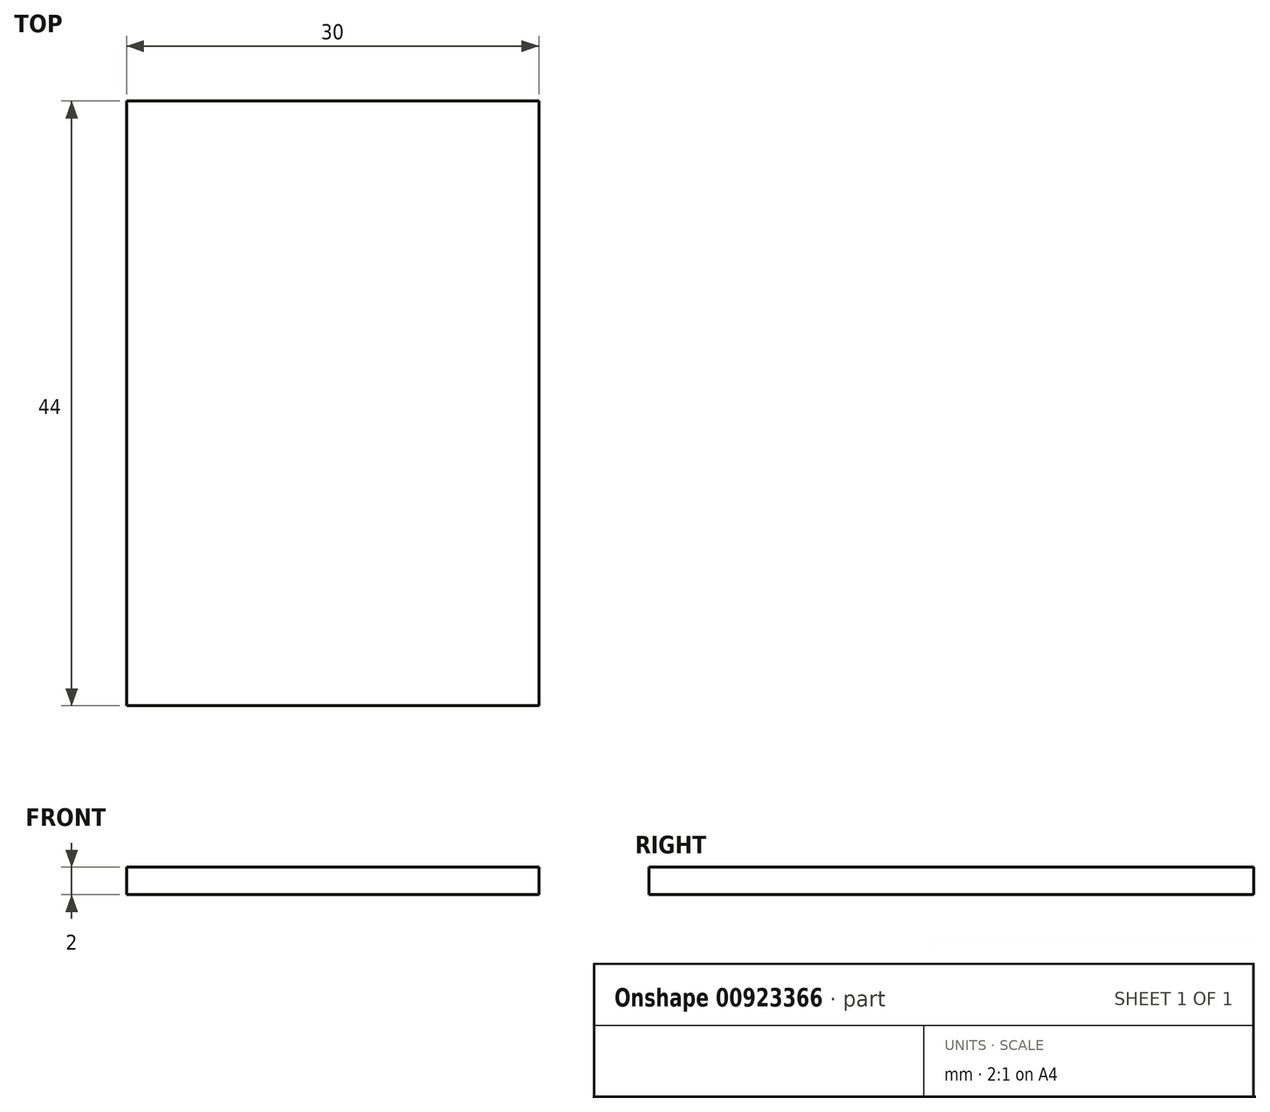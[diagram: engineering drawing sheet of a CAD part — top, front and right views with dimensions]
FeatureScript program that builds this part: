
annotation { "Feature Type Name" : "Feature", "Feature Type Description" : "" }
export const myFeature = defineFeature(function(context is Context, id is Id, definition is map)
    precondition{}
    {
        {
            var Q0;
            Q0=qCreatedBy(makeId("Top.planeOp"),FACE);
            var sketch = newSketch(context, id + "F0", { "sketchPlane" : qUnion([Q0])});
            skLineSegment(sketch, "E0.bottom", {"start": v(15, -22) * mm, "end": v(-15, -22) * mm});
            skLineSegment(sketch, "E0.top", {"start": v(15, 22) * mm, "end": v(-15, 22) * mm});
            skLineSegment(sketch, "E0.left", {"start": v(15, -22) * mm, "end": v(15, 22) * mm});
            skLineSegment(sketch, "E0.right", {"start": v(-15, -22) * mm, "end": v(-15, 22) * mm});
            skPoint(sketch, "E0.middle", {"position": v(0, 0) * mm});
            skSolve(sketch);
        }
        {
            var Q0;
            Q0 = qSketchRegion(id + "F0", true);
            extrude(context, id + "F1", {"entities" : qUnion([Q0]), "depth" : 2 * mm, "offsetDistance" : 25 * mm});
        }
    });
